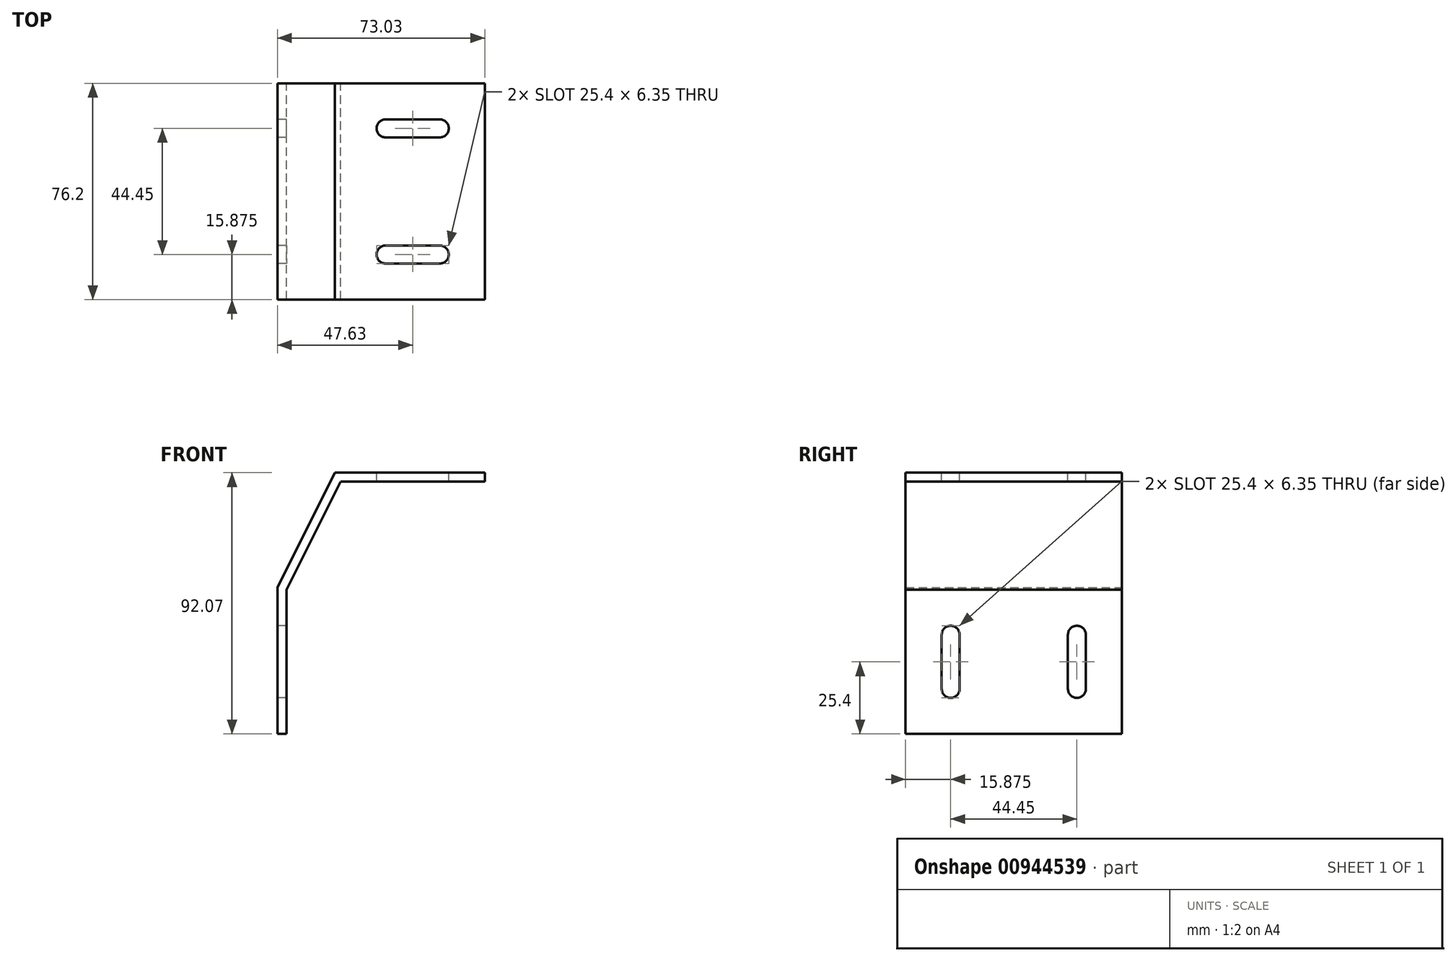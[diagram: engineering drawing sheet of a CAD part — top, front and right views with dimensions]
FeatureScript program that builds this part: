
annotation { "Feature Type Name" : "Feature", "Feature Type Description" : "" }
export const myFeature = defineFeature(function(context is Context, id is Id, definition is map)
    precondition{}
    {
        {
            var Q0;
            Q0=qCreatedBy(makeId("Front.planeOp"),FACE);
            var sketch = newSketch(context, id + "F0", { "sketchPlane" : qUnion([Q0])});
            skLineSegment(sketch, "E0", {"start": v(0, 0) * mm, "end": v(0, -50.8) * mm});
            skLineSegment(sketch, "E1", {"start": v(19.05, 38.1) * mm, "end": v(69.85, 38.1) * mm});
            skLineSegment(sketch, "E2", {"start": v(19.05, 38.1) * mm, "end": v(0, 0) * mm});
            skLineSegment(sketch, "E3", {"start": v(69.85, 38.1) * mm, "end": v(69.85, 41.28) * mm});
            skLineSegment(sketch, "E4", {"start": v(69.85, 41.28) * mm, "end": v(17.09, 41.28) * mm});
            skLineSegment(sketch, "E5", {"start": v(0, -50.8) * mm, "end": v(-3.18, -50.8) * mm});
            skLineSegment(sketch, "E6", {"start": v(-3.18, -50.8) * mm, "end": v(-3.18, 0.75) * mm});
            skLineSegment(sketch, "E7", {"start": v(-3.18, 0.75) * mm, "end": v(17.09, 41.28) * mm});
            skSolve(sketch);
        }
        {
            var Q0;
            Q0 = qSketchRegion(id + "F0", true);
            extrude(context, id + "F1", {"entities" : qUnion([Q0]), "depth" : 76.2 * mm, "offsetDistance" : 25.4 * mm});
        }
        {
            var Q0;
            Q0=makeQuery(id+"F1.opExtrude","SWEPT_FACE",FACE,{"disambiguationData":[OSD([sQuery(id+"F0.wireOp",EDGE,"E4")])]});
            var sketch = newSketch(context, id + "F2", { "sketchPlane" : qUnion([Q0])});
            skCircle(sketch, "E8", {"center": v(53.97, -15.87) * mm, "radius": 3.18 * mm});
            skCircle(sketch, "E9", {"center": v(34.92, -15.88) * mm, "radius": 3.18 * mm});
            skLineSegment(sketch, "E10", {"start": v(34.92, -12.7) * mm, "end": v(53.97, -12.7) * mm});
            skLineSegment(sketch, "E11", {"start": v(34.92, -19.05) * mm, "end": v(53.97, -19.05) * mm});
            skCircle(sketch, "E12", {"center": v(53.97, -60.33) * mm, "radius": 3.18 * mm});
            skCircle(sketch, "E13", {"center": v(34.92, -60.33) * mm, "radius": 3.18 * mm});
            skLineSegment(sketch, "E14", {"start": v(34.92, -57.15) * mm, "end": v(53.97, -57.15) * mm});
            skLineSegment(sketch, "E15", {"start": v(34.92, -63.5) * mm, "end": v(53.97, -63.5) * mm});
            skSolve(sketch);
        }
        {
            var Q0;
            {var subQ0=sQuery(id+"F2.wireOp",EDGE,"E8");var subQ1=makeQuery(id+"F2.imprint","INTERSECT",VERTEX,{"derivedFrom":[subQ0,sQuery(id+"F2.wireOp",EDGE,"E10")]});Q0=makeQuery(id+"F2.imprint","IMPRINT",FACE,{"disambiguationData":[TD([[makeQuery(id+"F2.imprint","IMPRINT",EDGE,{"disambiguationData":[TD([[subQ1,-1.0]])],"derivedFrom":subQ0}),1.0]])]});}
            var Q1;
            {var subQ0=sQuery(id+"F2.wireOp",EDGE,"E10");Q1=makeQuery(id+"F2.imprint","IMPRINT",FACE,{"disambiguationData":[TD([[makeQuery(id+"F2.imprint","IMPRINT",EDGE,{"derivedFrom":subQ0}),-1.0]])]});}
            var Q2;
            {var subQ0=sQuery(id+"F2.wireOp",EDGE,"E9");var subQ1=makeQuery(id+"F2.imprint","INTERSECT",VERTEX,{"derivedFrom":[subQ0,sQuery(id+"F2.wireOp",EDGE,"E10")]});Q2=makeQuery(id+"F2.imprint","IMPRINT",FACE,{"disambiguationData":[TD([[makeQuery(id+"F2.imprint","IMPRINT",EDGE,{"disambiguationData":[TD([[subQ1,-1.0]])],"derivedFrom":subQ0}),1.0]])]});}
            extrude(context, id + "F3", {"entities" : qUnion([Q0, Q1, Q2]), "operationType" : NewBodyOperationType.REMOVE, "endBound" : BoundingType.THROUGH_ALL, "oppositeDirection" : true, "depth" : 25.4 * mm, "offsetDistance" : 25.4 * mm});
        }
        {
            var Q0;
            {var subQ0=sQuery(id+"F2.wireOp",EDGE,"E13");var subQ1=makeQuery(id+"F2.imprint","INTERSECT",VERTEX,{"derivedFrom":[subQ0,sQuery(id+"F2.wireOp",EDGE,"E14")]});Q0=makeQuery(id+"F2.imprint","IMPRINT",FACE,{"disambiguationData":[TD([[makeQuery(id+"F2.imprint","IMPRINT",EDGE,{"disambiguationData":[TD([[subQ1,-1.0]])],"derivedFrom":subQ0}),1.0]])]});}
            var Q1;
            {var subQ0=sQuery(id+"F2.wireOp",EDGE,"E12");var subQ1=makeQuery(id+"F2.imprint","INTERSECT",VERTEX,{"derivedFrom":[subQ0,sQuery(id+"F2.wireOp",EDGE,"E14")]});Q1=makeQuery(id+"F2.imprint","IMPRINT",FACE,{"disambiguationData":[TD([[makeQuery(id+"F2.imprint","IMPRINT",EDGE,{"disambiguationData":[TD([[subQ1,-1.0]])],"derivedFrom":subQ0}),1.0]])]});}
            var Q2;
            {var subQ0=sQuery(id+"F2.wireOp",EDGE,"E14");Q2=makeQuery(id+"F2.imprint","IMPRINT",FACE,{"disambiguationData":[TD([[makeQuery(id+"F2.imprint","IMPRINT",EDGE,{"derivedFrom":subQ0}),-1.0]])]});}
            extrude(context, id + "F4", {"entities" : qUnion([Q0, Q1, Q2]), "operationType" : NewBodyOperationType.REMOVE, "endBound" : BoundingType.THROUGH_ALL, "oppositeDirection" : true, "depth" : 25.4 * mm, "offsetDistance" : 25.4 * mm});
        }
        {
            var Q0;
            Q0=makeQuery(id+"F1.opExtrude","SWEPT_FACE",FACE,{"disambiguationData":[OSD([sQuery(id+"F0.wireOp",EDGE,"E6")])]});
            var sketch = newSketch(context, id + "F5", { "sketchPlane" : qUnion([Q0])});
            skLineSegment(sketch, "E16.bottom", {"start": v(12.7, -34.93) * mm, "end": v(19.05, -34.93) * mm});
            skLineSegment(sketch, "E16.top", {"start": v(12.7, -15.88) * mm, "end": v(19.05, -15.88) * mm});
            skLineSegment(sketch, "E16.left", {"start": v(12.7, -34.93) * mm, "end": v(12.7, -15.88) * mm});
            skLineSegment(sketch, "E16.right", {"start": v(19.05, -34.93) * mm, "end": v(19.05, -15.88) * mm});
            skArc(sketch, "E17", {"start": v(19.05, -15.88) * mm, "mid": v(15.88, -12.7) * mm, "end": v(12.7, -15.88) * mm});
            skArc(sketch, "E18", {"start": v(12.7, -34.93) * mm, "mid": v(15.88, -38.1) * mm, "end": v(19.05, -34.93) * mm});
            skSolve(sketch);
        }
        {
            var Q0;
            Q0=makeQuery(id+"F5.imprint","IMPRINT",FACE,{"disambiguationData":[TD([[makeQuery(id+"F5.imprint","IMPRINT",EDGE,{"derivedFrom":sQuery(id+"F5.wireOp",EDGE,"E16.bottom")}),-1.0]])]});
            var Q1;
            Q1=makeQuery(id+"F5.imprint","IMPRINT",FACE,{"disambiguationData":[TD([[makeQuery(id+"F5.imprint","IMPRINT",EDGE,{"derivedFrom":sQuery(id+"F5.wireOp",EDGE,"E16.top")}),1.0]])]});
            var Q2;
            Q2=makeQuery(id+"F5.imprint","IMPRINT",FACE,{"disambiguationData":[TD([[makeQuery(id+"F5.imprint","IMPRINT",EDGE,{"derivedFrom":sQuery(id+"F5.wireOp",EDGE,"E16.bottom")}),1.0]])]});
            extrude(context, id + "F6", {"entities" : qUnion([Q0, Q1, Q2]), "operationType" : NewBodyOperationType.REMOVE, "endBound" : BoundingType.THROUGH_ALL, "oppositeDirection" : true, "depth" : 25.4 * mm, "offsetDistance" : 25.4 * mm});
        }
        {
            var Q0;
            Q0=makeQuery(id+"F1.opExtrude","SWEPT_FACE",FACE,{"disambiguationData":[OSD([sQuery(id+"F0.wireOp",EDGE,"E6")])]});
            var sketch = newSketch(context, id + "F7", { "sketchPlane" : qUnion([Q0])});
            skLineSegment(sketch, "E19.bottom", {"start": v(63.5, -34.93) * mm, "end": v(57.15, -34.93) * mm});
            skLineSegment(sketch, "E19.top", {"start": v(63.5, -15.88) * mm, "end": v(57.15, -15.88) * mm});
            skLineSegment(sketch, "E19.left", {"start": v(63.5, -34.92) * mm, "end": v(63.5, -15.88) * mm});
            skLineSegment(sketch, "E19.right", {"start": v(57.15, -34.92) * mm, "end": v(57.15, -15.88) * mm});
            skArc(sketch, "E20", {"start": v(57.15, -34.92) * mm, "mid": v(60.33, -38.1) * mm, "end": v(63.5, -34.92) * mm});
            skArc(sketch, "E21", {"start": v(63.5, -15.88) * mm, "mid": v(60.33, -12.7) * mm, "end": v(57.15, -15.88) * mm});
            skSolve(sketch);
        }
        {
            var Q0;
            Q0=makeQuery(id+"F7.imprint","IMPRINT",FACE,{"disambiguationData":[TD([[makeQuery(id+"F7.imprint","IMPRINT",EDGE,{"derivedFrom":sQuery(id+"F7.wireOp",EDGE,"E19.top")}),-1.0]])]});
            var Q1;
            Q1=makeQuery(id+"F7.imprint","IMPRINT",FACE,{"disambiguationData":[TD([[makeQuery(id+"F7.imprint","IMPRINT",EDGE,{"derivedFrom":sQuery(id+"F7.wireOp",EDGE,"E19.bottom")}),1.0]])]});
            var Q2;
            Q2=makeQuery(id+"F7.imprint","IMPRINT",FACE,{"disambiguationData":[TD([[makeQuery(id+"F7.imprint","IMPRINT",EDGE,{"derivedFrom":sQuery(id+"F7.wireOp",EDGE,"E19.bottom")}),-1.0]])]});
            extrude(context, id + "F8", {"entities" : qUnion([Q0, Q1, Q2]), "operationType" : NewBodyOperationType.REMOVE, "endBound" : BoundingType.THROUGH_ALL, "oppositeDirection" : true, "depth" : 25.4 * mm, "offsetDistance" : 25.4 * mm});
        }
    });
